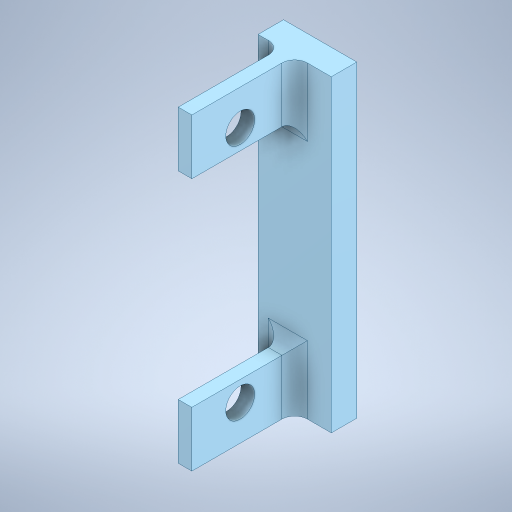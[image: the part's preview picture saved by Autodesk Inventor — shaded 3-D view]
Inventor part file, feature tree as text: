
AUTODESK INVENTOR PART (.ipt)
format: ipt  version: 2024 (Build 280153000, 153)  size: 704,000 bytes
history: native  units: mm
features: sketch x7, extrude x6, move_body x4, thicken_offset x4, other x2, boolean_combine x1, fillet x1
ambient origin geometry x8: Origin, YZ Plane, XZ Plane, XY Plane, X Axis, Y Axis, Z Axis, Center Point
bodies: Solid1 (feature_tree), Solid2 (feature_tree), Solid3 (feature_tree)
feature tree (25):
  extrude  "Extrusion1"  Depth=3.0mm
  other  "Part 1:1"
  move_body  "Move Body2"
  extrude  "Extrusion2"  Depth=5.69mm
  extrude  "Extrusion3"  TaperAngle=0.0deg  [1 undecoded]
  move_body  "Move Body3"
  extrude  "Extrusion4"  Depth=1.5mm
  move_body  "Move Body4"
  move_body  "Move Body5"
  boolean_combine  "Combine3"
  extrude  "Extrusion5"  Depth=10.0mm
  extrude  "Extrusion6"  Depth=3.0mm TaperAngle=0.0deg
  fillet  "Fillet1"  [1 undecoded]
  thicken_offset  "Thicken1"
  thicken_offset  "Thicken2"
  sketch  "Sketch12"  dims[d29=0.0mm d30=0.0mm d31=-10.0mm d32=0.0mm d33=100.0mm d34=0.0mm d35=0.0mm d36=0.0mm d37=10.0mm d38=0.0mm d39=0.0mm d40=13.0mm d41=3.0mm d42=0.0mm d43=3.0mm d44=0.0mm d45=1.5mm d58=0.2mm d59=0.2mm d60=0.2mm d61=0.2mm d62=2.0mm d63=2.0mm d64=2.0mm d65=2.0mm]
  thicken_offset  "Thicken3"
  thicken_offset  "Thicken4"
  sketch  "Sketch3"  dims[d1=3.0mm d8=28.0mm]
  sketch  "Sketch5"  dims[d9=11.65mm d10=5.69mm]
  sketch  "Sketch6"  dims[d11=10.0mm d12=0.0mm d16=0.0mm d17=0.0mm d18=-10.0mm]
  sketch  "Sketch7"  dims[d19=1.5mm d20=17.65mm]
  sketch  "Sketch9"  dims[d21=10.0mm d22=0.0mm d23=32.3mm]
  sketch  "Sketch10"  dims[d26=4.312299mm d27=3.0mm d28=0.0mm]
  other  "Part 1"
note: 2 required parameter values undecoded (feature->parameter linkage not recoverable at this tier; creation-order binding heuristic only, values carry confidence <= 0.55)
